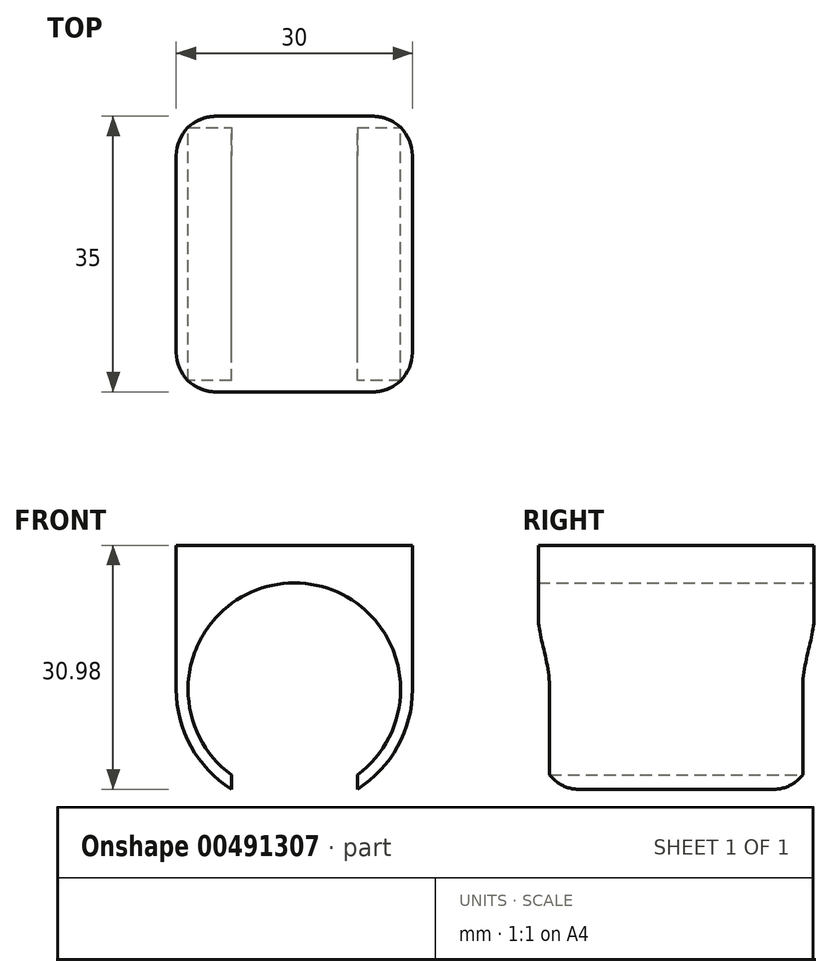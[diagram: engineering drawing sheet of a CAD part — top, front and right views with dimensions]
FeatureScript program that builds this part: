
annotation { "Feature Type Name" : "Feature", "Feature Type Description" : "" }
export const myFeature = defineFeature(function(context is Context, id is Id, definition is map)
    precondition{}
    {
        {
            var Q0;
            Q0=qCreatedBy(makeId("Front.planeOp"),FACE);
            var sketch = newSketch(context, id + "F0", { "sketchPlane" : qUnion([Q0])});
            skArc(sketch, "E0", {"start": v(8, -10.87) * mm, "mid": v(0, 13.5) * mm, "end": v(-8, -10.87) * mm});
            skArc(sketch, "E1", {"start": v(8, -12.69) * mm, "mid": v(13.13, -7.25) * mm, "end": v(15, 0) * mm});
            skLineSegment(sketch, "E2", {"start": v(-8, -12.69) * mm, "end": v(-8, -10.87) * mm});
            skLineSegment(sketch, "E3.MirrorCS", {"start": v(8, -12.69) * mm, "end": v(8, -10.87) * mm});
            skPoint(sketch, "E4.MirrorCS.end.orphan", {"position": v(0, -6.64) * mm});
            skPoint(sketch, "E4.MirrorCS.start.orphan", {"position": v(8, -6.64) * mm});
            skPoint(sketch, "E5.orphan", {"position": v(-8, -6.64) * mm});
            skPoint(sketch, "E6.end.orphan", {"position": v(-8, -18.93) * mm});
            skPoint(sketch, "E7.end.orphan", {"position": v(0, -18.93) * mm});
            skLineSegment(sketch, "E8", {"start": v(-15, 0) * mm, "end": v(-15, 18.29) * mm});
            skLineSegment(sketch, "E9", {"start": v(-15, 18.29) * mm, "end": v(15, 18.29) * mm});
            skLineSegment(sketch, "E10", {"start": v(15, 0) * mm, "end": v(15, 18.29) * mm});
            skPoint(sketch, "E11.orphan", {"position": v(15.3, 18.29) * mm});
            skArc(sketch, "E12.trimOffspring", {"start": v(-15, 0) * mm, "mid": v(-13.13, -7.25) * mm, "end": v(-8, -12.69) * mm});
            skSolve(sketch);
        }
        {
            var Q0;
            Q0 = qSketchRegion(id + "F0", true);
            extrude(context, id + "F1", {"entities" : qUnion([Q0]), "depth" : 35 * mm});
        }
        {
            var Q0;
            Q0=makeQuery(id+"F1.opExtrude","CAP_EDGE",EDGE,{"disambiguationData":[OSD([sQuery(id+"F0.wireOp",EDGE,"E10")])],"isStart":false});
            var Q1;
            Q1=makeQuery(id+"F1.opExtrude","CAP_EDGE",EDGE,{"disambiguationData":[OSD([sQuery(id+"F0.wireOp",EDGE,"E8")])],"isStart":false});
            var Q2;
            Q2=makeQuery(id+"F1.opExtrude","CAP_EDGE",EDGE,{"disambiguationData":[OSD([sQuery(id+"F0.wireOp",EDGE,"E10")])],"isStart":true});
            var Q3;
            Q3=makeQuery(id+"F1.opExtrude","CAP_EDGE",EDGE,{"disambiguationData":[OSD([sQuery(id+"F0.wireOp",EDGE,"E8")])],"isStart":true});
            fillet(context, id + "F2", {"entities" : qUnion([Q0, Q1, Q2, Q3]), "radius" : 5 * mm, "tangentPropagation" : true, "allowEdgeOverflow" : false});
        }
    });
